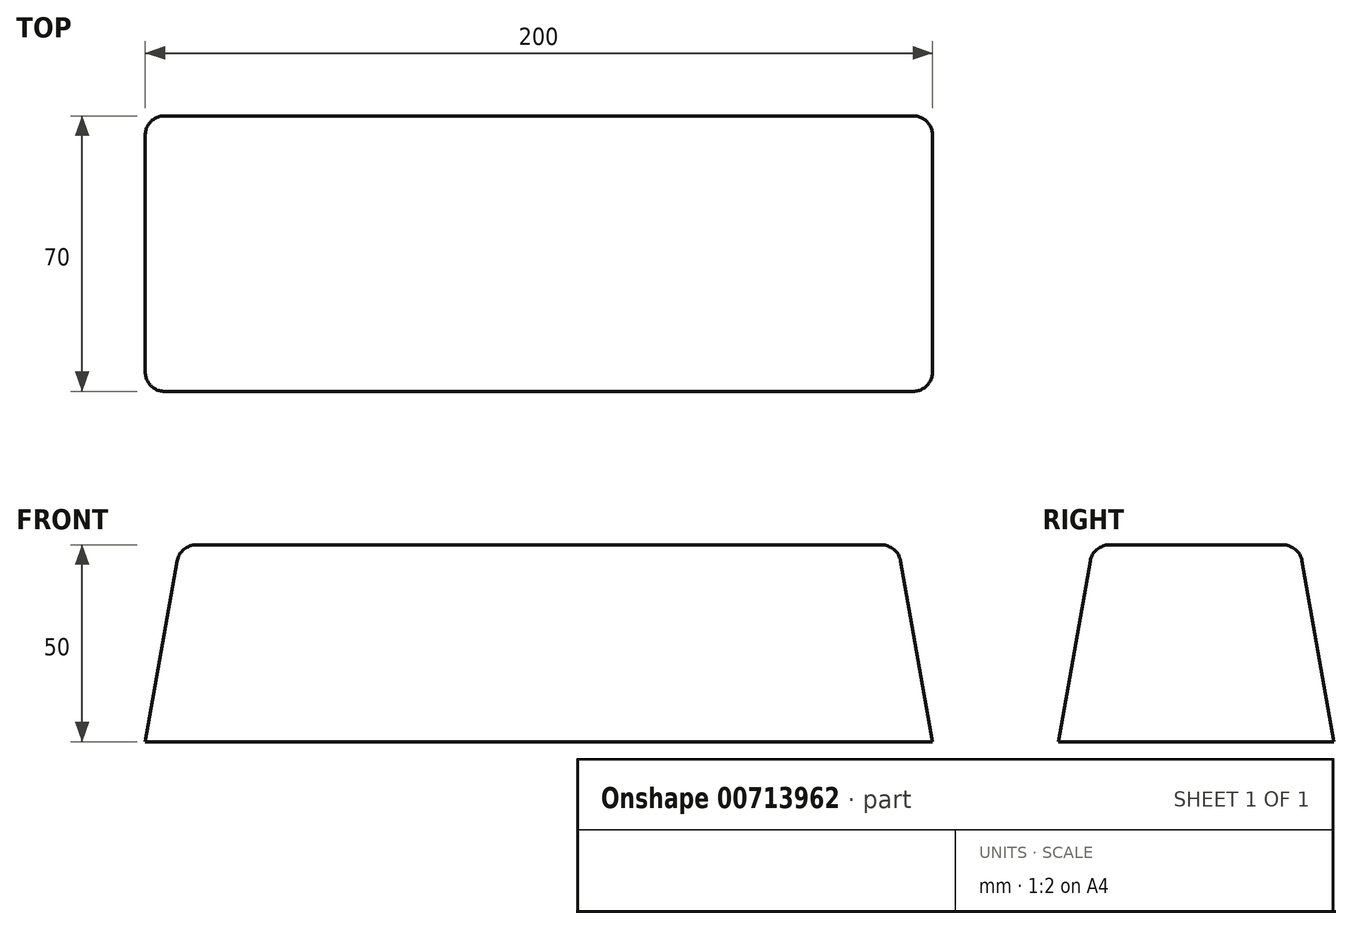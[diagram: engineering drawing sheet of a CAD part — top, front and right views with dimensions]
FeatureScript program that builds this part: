
annotation { "Feature Type Name" : "Feature", "Feature Type Description" : "" }
export const myFeature = defineFeature(function(context is Context, id is Id, definition is map)
    precondition{}
    {
        {
            var Q0;
            Q0=qCreatedBy(makeId("Top.planeOp"),FACE);
            var sketch = newSketch(context, id + "F0", { "sketchPlane" : qUnion([Q0])});
            skLineSegment(sketch, "E0.bottom", {"start": v(-100, 35) * mm, "end": v(100, 35) * mm});
            skLineSegment(sketch, "E0.top", {"start": v(-100, -35) * mm, "end": v(100, -35) * mm});
            skLineSegment(sketch, "E0.left", {"start": v(-100, 35) * mm, "end": v(-100, -35) * mm});
            skLineSegment(sketch, "E0.right", {"start": v(100, 35) * mm, "end": v(100, -35) * mm});
            skSolve(sketch);
        }
        {
            var Q0;
            Q0=makeQuery(id+"F0.imprint","IMPRINT",FACE,{"disambiguationData":[TD([[makeQuery(id+"F0.imprint","IMPRINT",EDGE,{"derivedFrom":sQuery(id+"F0.wireOp",EDGE,"E0.bottom")}),-1.0]])]});
            extrude(context, id + "F1", {"entities" : qUnion([Q0]), "depth" : 50 * mm, "offsetDistance" : 25 * mm, "hasDraft" : true, "draftAngle" : 10 * degree, "draftPullDirection" : true});
        }
        {
            var Q0;
            Q0=makeQuery(id+"F1.opExtrude","CAP_EDGE",EDGE,{"disambiguationData":[OSD([sQuery(id+"F0.wireOp",EDGE,"E0.left")])],"isStart":false});
            var Q1;
            Q1=makeQuery(id+"F1.opExtrude","CAP_EDGE",EDGE,{"disambiguationData":[OSD([sQuery(id+"F0.wireOp",EDGE,"E0.top")])],"isStart":false});
            var Q2;
            Q2=makeQuery(id+"F1.opExtrude","SWEPT_EDGE",EDGE,{"disambiguationData":[OSD([sQuery(id+"F0.wireOp",EDGE,"E0.top"),sQuery(id+"F0.wireOp",EDGE,"E0.left")])]});
            var Q3;
            Q3=makeQuery(id+"F1.opExtrude","CAP_EDGE",EDGE,{"disambiguationData":[OSD([sQuery(id+"F0.wireOp",EDGE,"E0.bottom")])],"isStart":false});
            var Q4;
            Q4=makeQuery(id+"F1.opExtrude","CAP_EDGE",EDGE,{"disambiguationData":[OSD([sQuery(id+"F0.wireOp",EDGE,"E0.right")])],"isStart":false});
            var Q5;
            Q5=makeQuery(id+"F1.opExtrude","SWEPT_EDGE",EDGE,{"disambiguationData":[OSD([sQuery(id+"F0.wireOp",EDGE,"E0.top"),sQuery(id+"F0.wireOp",EDGE,"E0.right")])]});
            var Q6;
            Q6=makeQuery(id+"F1.opExtrude","SWEPT_EDGE",EDGE,{"disambiguationData":[OSD([sQuery(id+"F0.wireOp",EDGE,"E0.bottom"),sQuery(id+"F0.wireOp",EDGE,"E0.left")])]});
            var Q7;
            Q7=makeQuery(id+"F1.opExtrude","SWEPT_EDGE",EDGE,{"disambiguationData":[OSD([sQuery(id+"F0.wireOp",EDGE,"E0.bottom"),sQuery(id+"F0.wireOp",EDGE,"E0.right")])]});
            fillet(context, id + "F2", {"entities" : qUnion([Q0, Q1, Q2, Q3, Q4, Q5, Q6, Q7]), "radius" : 5 * mm, "tangentPropagation" : true, "allowEdgeOverflow" : false});
        }
    });
